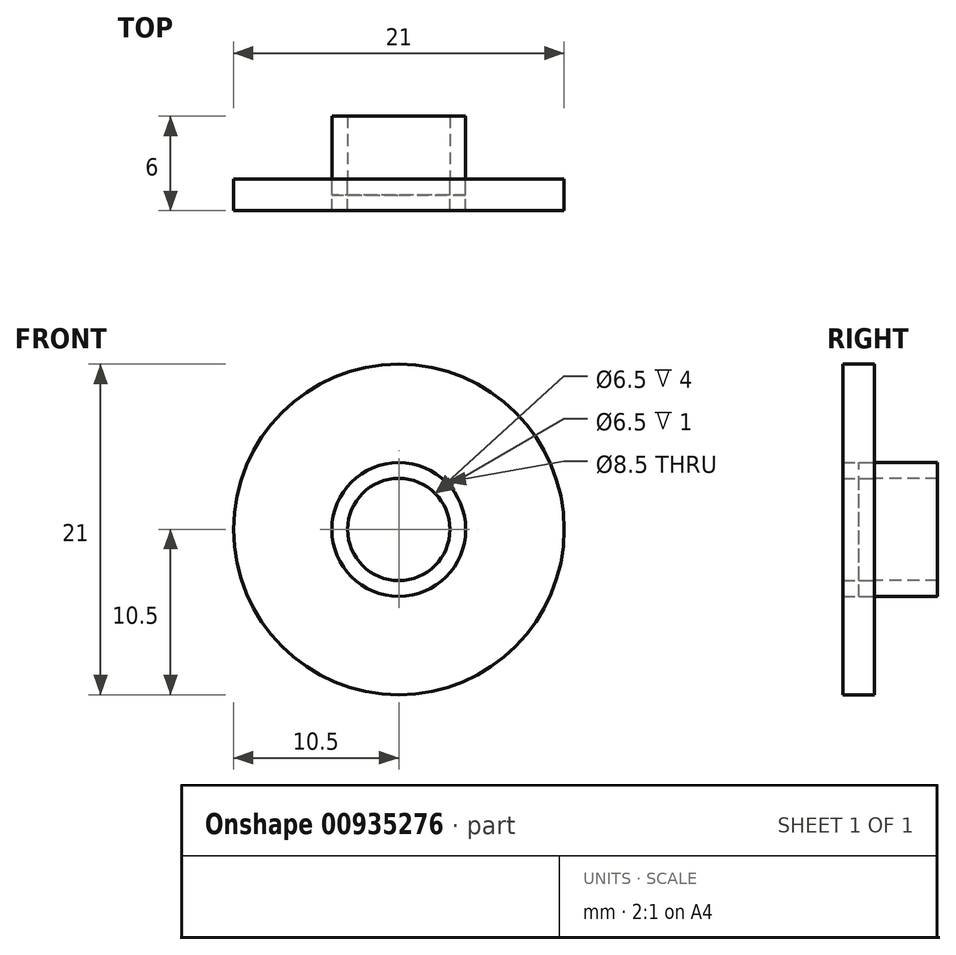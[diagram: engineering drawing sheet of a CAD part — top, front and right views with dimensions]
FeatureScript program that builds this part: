
annotation { "Feature Type Name" : "Feature", "Feature Type Description" : "" }
export const myFeature = defineFeature(function(context is Context, id is Id, definition is map)
    precondition{}
    {
        {
            var Q0;
            Q0=qCreatedBy(makeId("Front.planeOp"),FACE);
            var sketch = newSketch(context, id + "F0", { "sketchPlane" : qUnion([Q0])});
            skCircle(sketch, "E0", {"center": v(0, 0) * mm, "radius": 10.5 * mm});
            skCircle(sketch, "E1", {"center": v(0, 0) * mm, "radius": 4.25 * mm});
            skCircle(sketch, "E2", {"center": v(0, 0) * mm, "radius": 3.25 * mm});
            skSolve(sketch);
        }
        {
            var Q0;
            Q0=makeQuery(id+"F0.imprint","IMPRINT",FACE,{"disambiguationData":[TD([[makeQuery(id+"F0.imprint","IMPRINT",EDGE,{"derivedFrom":sQuery(id+"F0.wireOp",EDGE,"E0")}),1.0]])]});
            var Q1;
            Q1=makeQuery(id+"F0.imprint","IMPRINT",FACE,{"disambiguationData":[TD([[makeQuery(id+"F0.imprint","IMPRINT",EDGE,{"derivedFrom":sQuery(id+"F0.wireOp",EDGE,"E2")}),1.0]])]});
            extrude(context, id + "F1", {"entities" : qUnion([Q0, Q1]), "depth" : 2 * mm, "offsetDistance" : 25 * mm});
        }
        {
            var Q0;
            Q0=makeQuery(id+"F0.imprint","IMPRINT",FACE,{"disambiguationData":[TD([[makeQuery(id+"F0.imprint","IMPRINT",EDGE,{"derivedFrom":sQuery(id+"F0.wireOp",EDGE,"E1")}),1.0]])]});
            extrude(context, id + "F2", {"entities" : qUnion([Q0]), "oppositeDirection" : true, "depth" : 4 * mm, "offsetDistance" : 25 * mm});
        }
        {
            var Q0;
            Q0=makeQuery(id+"F0.imprint","IMPRINT",FACE,{"disambiguationData":[TD([[makeQuery(id+"F0.imprint","IMPRINT",EDGE,{"derivedFrom":sQuery(id+"F0.wireOp",EDGE,"E1")}),1.0]])]});
            extrude(context, id + "F3", {"entities" : qUnion([Q0]), "depth" : 1 * mm, "offsetDistance" : 25 * mm});
        }
    });
